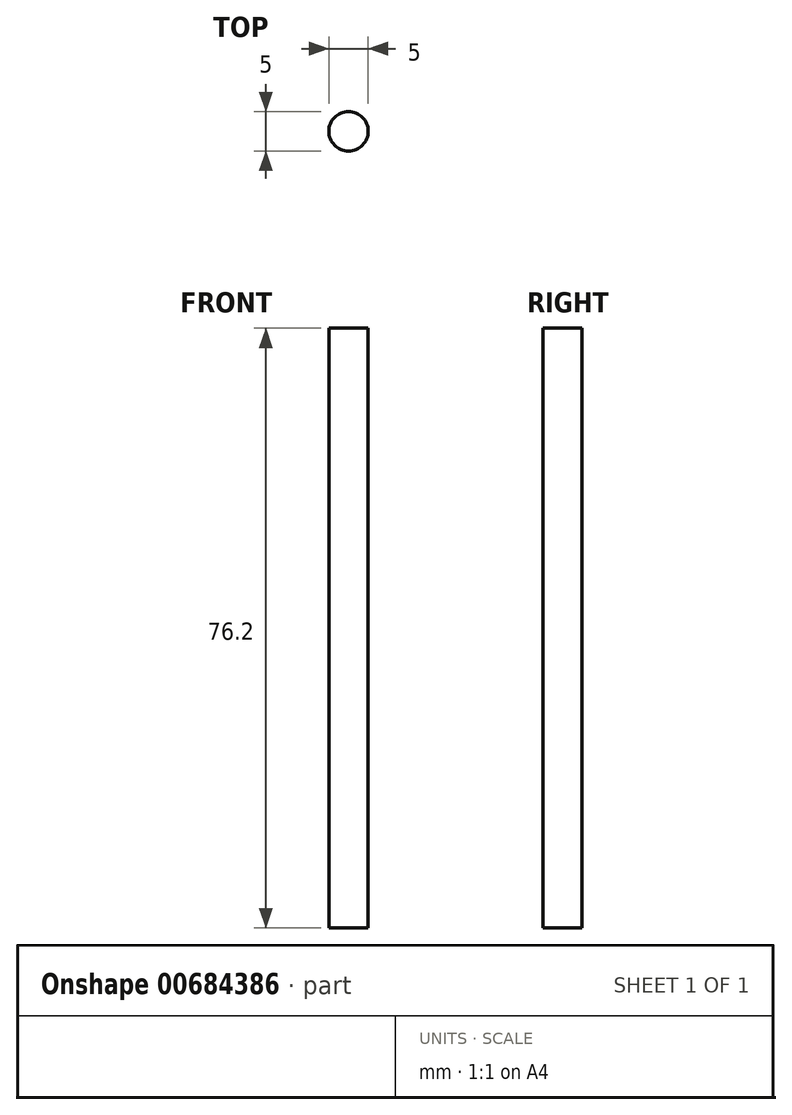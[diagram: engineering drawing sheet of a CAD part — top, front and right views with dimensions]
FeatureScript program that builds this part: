
annotation { "Feature Type Name" : "Feature", "Feature Type Description" : "" }
export const myFeature = defineFeature(function(context is Context, id is Id, definition is map)
    precondition{}
    {
        {
            var Q0;
            Q0=qCreatedBy(makeId("Top.planeOp"),FACE);
            var sketch = newSketch(context, id + "F0", { "sketchPlane" : qUnion([Q0])});
            skCircle(sketch, "E0", {"center": v(0, 0) * mm, "radius": 2.5 * mm});
            skSolve(sketch);
        }
        {
            var Q0;
            Q0=makeQuery(id+"F0.imprint","IMPRINT",FACE,{"disambiguationData":[TD([[makeQuery(id+"F0.imprint","IMPRINT",EDGE,{"derivedFrom":sQuery(id+"F0.wireOp",EDGE,"E0")}),1.0]])]});
            extrude(context, id + "F1", {"entities" : qUnion([Q0]), "depth" : 76.2 * mm, "offsetDistance" : 25.4 * mm});
        }
    });
